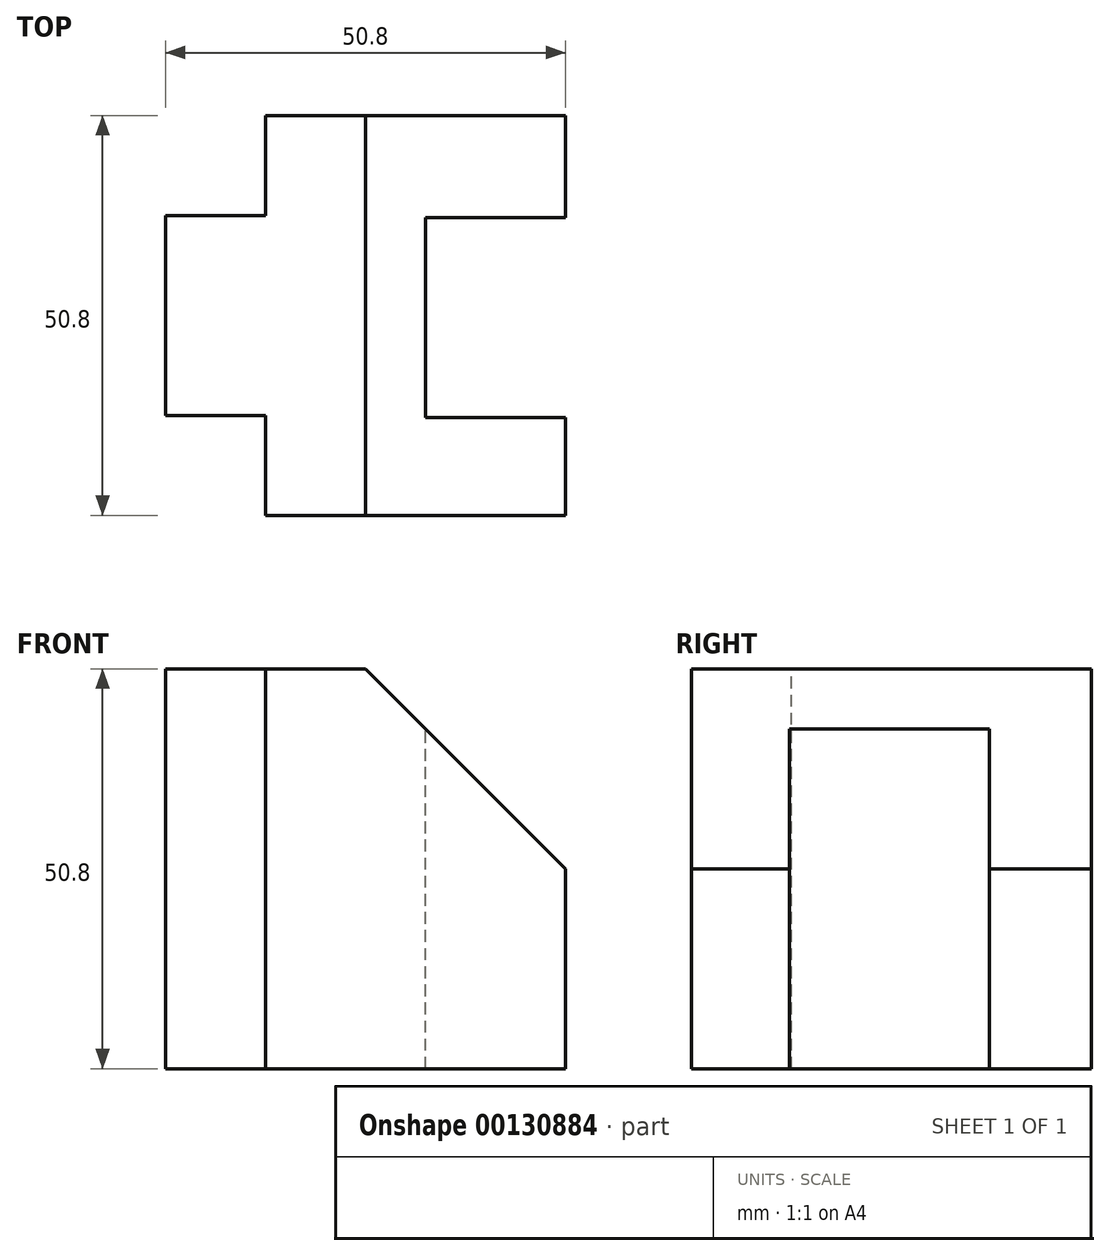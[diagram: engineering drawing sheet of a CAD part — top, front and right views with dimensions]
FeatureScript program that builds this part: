
annotation { "Feature Type Name" : "Feature", "Feature Type Description" : "" }
export const myFeature = defineFeature(function(context is Context, id is Id, definition is map)
    precondition{}
    {
        {
            var Q0;
            Q0=qCreatedBy(makeId("Front.planeOp"),FACE);
            var sketch = newSketch(context, id + "F0", { "sketchPlane" : qUnion([Q0])});
            skLineSegment(sketch, "E0", {"start": v(0, 0) * mm, "end": v(0, 50.8) * mm});
            skLineSegment(sketch, "E1", {"start": v(0, 50.8) * mm, "end": v(25.4, 50.8) * mm});
            skLineSegment(sketch, "E2", {"start": v(25.4, 50.8) * mm, "end": v(50.8, 25.4) * mm});
            skLineSegment(sketch, "E3", {"start": v(50.8, 25.4) * mm, "end": v(50.8, 0) * mm});
            skLineSegment(sketch, "E4", {"start": v(50.8, 0) * mm, "end": v(0, 0) * mm});
            skLineSegment(sketch, "E5", {"start": v(12.7, 0) * mm, "end": v(12.7, 50.8) * mm});
            skLineSegment(sketch, "E6", {"start": v(33.02, 43.18) * mm, "end": v(33.02, 0) * mm, "construction": true});
            skSolve(sketch);
        }
        {
            var Q0;
            {var subQ0=sQuery(id+"F0.wireOp",EDGE,"E0");Q0=makeQuery(id+"F0.imprint","IMPRINT",FACE,{"disambiguationData":[TD([[makeQuery(id+"F0.imprint","IMPRINT",EDGE,{"derivedFrom":subQ0}),-1.0]])]});}
            extrude(context, id + "F1", {"entities" : qUnion([Q0]), "endBound" : BoundingType.SYMMETRIC, "depth" : 25.4 * mm});
        }
        {
            var Q0;
            Q0 = qSketchRegion(id + "F0", true);
            extrude(context, id + "F2", {"entities" : qUnion([Q0]), "operationType" : NewBodyOperationType.ADD, "endBound" : BoundingType.SYMMETRIC, "depth" : 25.4 * mm});
        }
        {
            var Q0;
            {var subQ3=sQuery(id+"F0.wireOp",EDGE,"E2");Q0=makeQuery(id+"F0.imprint","IMPRINT",FACE,{"disambiguationData":[TD([[makeQuery(id+"F0.imprint","IMPRINT",EDGE,{"derivedFrom":subQ3}),-1.0]])]});}
            extrude(context, id + "F3", {"entities" : qUnion([Q0]), "operationType" : NewBodyOperationType.ADD, "endBound" : BoundingType.SYMMETRIC, "depth" : 50.8 * mm});
        }
        {
            var Q0;
            {var subQ0=sQuery(id+"F0.wireOp",EDGE,"E1");Q0=makeQuery(id+"F3.boolean.opBoolean","MERGE",FACE,{"derivedFrom":[makeQuery(id+"F2.boolean.opBoolean","MERGE",FACE,{"derivedFrom":[makeQuery(id+"F1.opExtrude","SWEPT_FACE",FACE,{"disambiguationData":[OSD([subQ0])]}),makeQuery(id+"F2.opExtrude","SWEPT_FACE",FACE,{"disambiguationData":[OSD([subQ0])]})]}),makeQuery(id+"F3.opExtrude","SWEPT_FACE",FACE,{"disambiguationData":[OSD([subQ0])]})]});}
            var sketch = newSketch(context, id + "F4", { "sketchPlane" : qUnion([Q0])});
            skLineSegment(sketch, "E7", {"start": v(25.4, 12.42) * mm, "end": v(50.8, 12.42) * mm, "construction": true});
            skLineSegment(sketch, "E8", {"start": v(25.4, -12.98) * mm, "end": v(50.8, -12.98) * mm, "construction": true});
            skLineSegment(sketch, "E9", {"start": v(33.02, 12.42) * mm, "end": v(33.02, -12.98) * mm});
            skLineSegment(sketch, "E10", {"start": v(33.02, -12.98) * mm, "end": v(50.8, -12.98) * mm});
            skLineSegment(sketch, "E11", {"start": v(50.8, 12.42) * mm, "end": v(33.02, 12.42) * mm});
            skLineSegment(sketch, "E12", {"start": v(50.8, 12.42) * mm, "end": v(50.8, -12.98) * mm});
            skSolve(sketch);
        }
        {
            var Q0;
            Q0=makeQuery(id+"F4.imprint","IMPRINT",FACE,{"disambiguationData":[TD([[makeQuery(id+"F4.imprint","IMPRINT",EDGE,{"derivedFrom":sQuery(id+"F4.wireOp",EDGE,"E9")}),1.0]])]});
            extrude(context, id + "F5", {"entities" : qUnion([Q0]), "operationType" : NewBodyOperationType.REMOVE, "endBound" : BoundingType.THROUGH_ALL, "oppositeDirection" : true, "depth" : 25.4 * mm});
        }
    });
